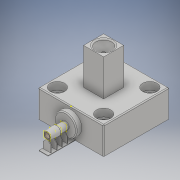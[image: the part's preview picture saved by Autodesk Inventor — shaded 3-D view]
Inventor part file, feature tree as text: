
AUTODESK INVENTOR PART (.ipt)
format: ipt  version: 2019 (Build 230136000, 136)  size: 391,680 bytes
history: native  units: mm
features: sketch x14, extrude x8, plane x7, projected_geometry x4, revolve x2, fillet x2, sweep x1, hole x1
ambient origin geometry x8: Origin, YZ Plane, XZ Plane, XY Plane, X Axis, Y Axis, Z Axis, Center Point
bodies: Solid1 (feature_tree)
feature tree (39):
  revolve  "Revolution1"  [1 undecoded]
  plane  "Work Plane1"
  extrude  "Extrusion1"  Depth=0.35mm
  plane  "Work Plane7"
  extrude  "Extrusion6"  Depth=0.75mm
  extrude  "Extrusion7"  TaperAngle=90.0deg  [1 undecoded]
  sketch  "Sketch17"  dims[d11=0.0mm d14=2.0mm d15=0.0mm d45=0.0mm]
  plane  "Work Plane8"
  sweep  "Sweep3"
  fillet  "Fillet1"  [1 undecoded]
  hole  "Hole3"  [1 undecoded]
  revolve  "Revolution2"  [1 undecoded]
  fillet  "Fillet2"  Radius=32.7mm
  plane  "Work Plane10"
  plane  "Work Plane11"
  plane  "Work Plane12"
  plane  "Work Plane13"
  extrude  "Extrusion8"  Depth=3.0mm
  extrude  "Extrusion9"  Depth=25.4mm
  extrude  "Extrusion10"  Depth=3.0mm
  extrude  "Extrusion11"  Depth=5.0mm
  extrude  "Extrusion12"  Depth=0.25mm
  sketch  "Sketch27"  dims[d85=5.08mm d86=1.15mm d87=0.25mm d88=0.25mm d89=90.0deg d90=0.5mm d92=0.0mm d93=-3.0mm d94=-6.0mm d95=-9.0mm d97=2.0mm d98=2.0mm d99=2.0mm d100=2.0mm d101=0.3mm d102=0.3mm d103=0.0mm d104=2.0mm d105=2.0mm d106=2.0mm d107=2.0mm d108=0.3mm d109=0.3mm d110=0.0mm d111=2.0mm d112=2.0mm d113=2.0mm d114=2.0mm d115=0.3mm d116=0.3mm d117=0.0mm d118=0.3mm d119=0.0mm d120=5.0mm d121=0.3mm d122=15.0mm d123=0.0mm d124=0.0mm]
  sketch  "Sketch1"  dims[d0=5.5mm d1=20.0mm]
  sketch  "Sketch2"  dims[d5=9.0mm d6=0.35mm]
  sketch  "Sketch11"  dims[d7=0.75mm d8=0.75mm]
  sketch  "Sketch16"  dims[d9=0.75mm d10=90.0deg]
  projected_geometry  "Projected Loop9"
  sketch  "Sketch18"  dims[d47=15.0mm d48=0.0mm d60=36.0mm]
  sketch  "Sketch19"  dims[d61=36.0mm d64=8.45mm d65=32.7mm d66=0.0mm]
  sketch  "Sketch21"  dims[d67=0.0mm d68=0.0mm d69=3.0mm]
  sketch  "Sketch22"  dims[d70=25.4mm d71=25.4mm]
  sketch  "Sketch23"  dims[d72=4.496mm d73=6.0mm d74=7.938mm d75=4.166mm d76=90.0deg d77=19.05mm d78=20.594885mm d79=3.0mm]
  projected_geometry  "Projected Loop10"
  sketch  "Sketch24"  dims[d80=6.0mm d81=5.0mm]
  projected_geometry  "Projected Loop11"
  sketch  "Sketch25"  dims[d82=1.8796mm d83=0.25mm]
  projected_geometry  "Projected Loop12"
  sketch  "Sketch26"  dims[d84=2.413mm]
note: 5 required parameter values undecoded (feature->parameter linkage not recoverable at this tier; creation-order binding heuristic only, values carry confidence <= 0.55)